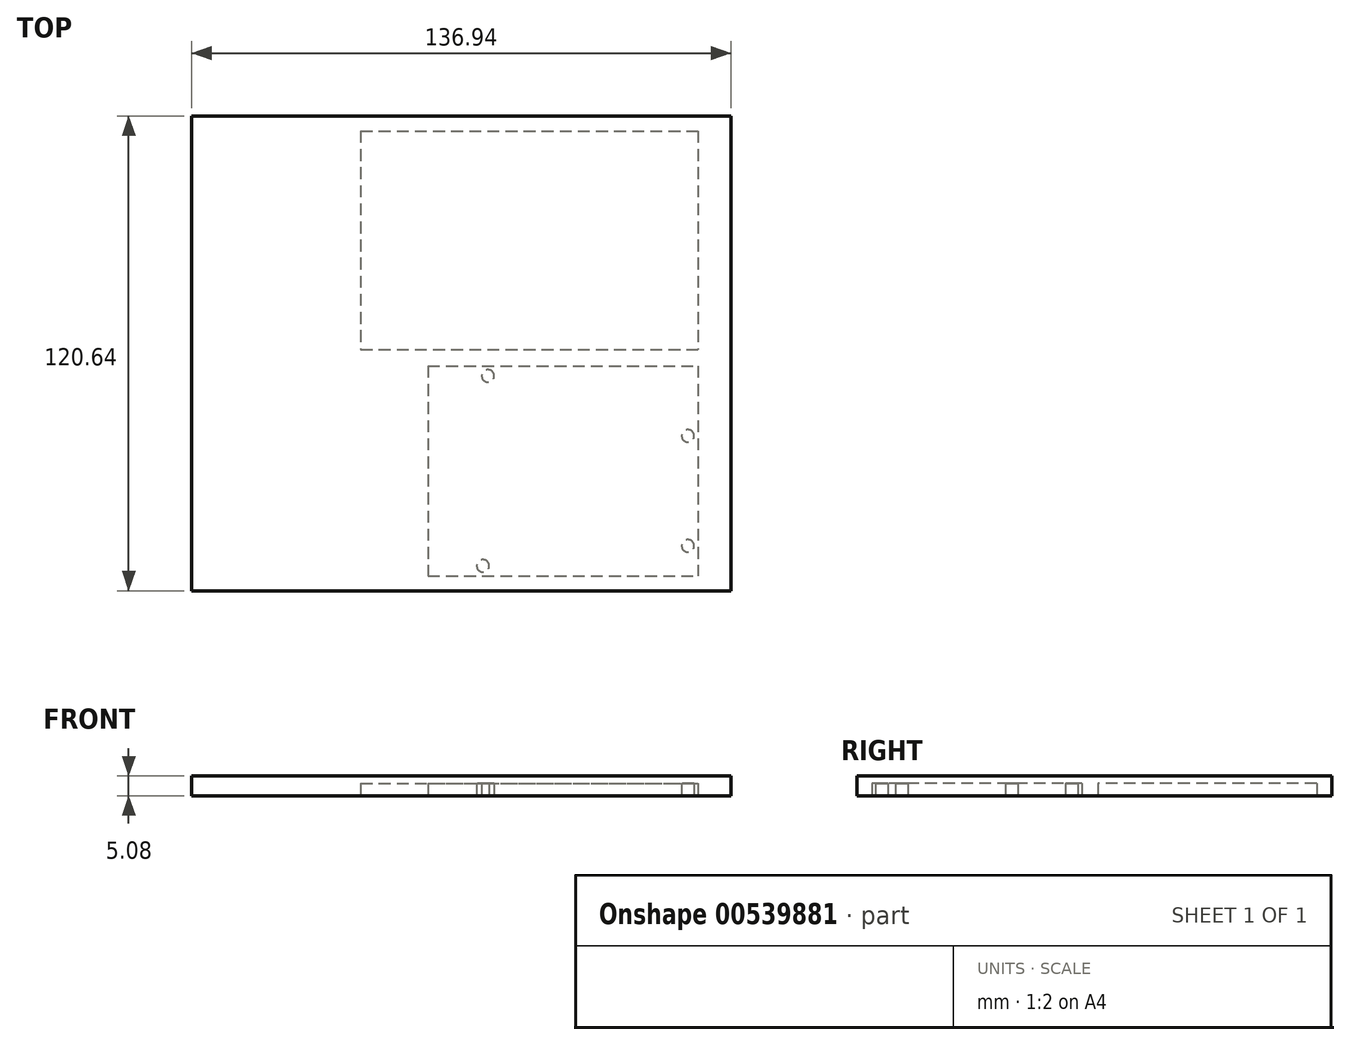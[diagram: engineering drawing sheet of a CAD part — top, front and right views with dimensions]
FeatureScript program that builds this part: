
annotation { "Feature Type Name" : "Feature", "Feature Type Description" : "" }
export const myFeature = defineFeature(function(context is Context, id is Id, definition is map)
    precondition{}
    {
        {
            var Q0;
            Q0=qCreatedBy(makeId("Top.planeOp"),FACE);
            var sketch = newSketch(context, id + "F0", { "sketchPlane" : qUnion([Q0])});
            skLineSegment(sketch, "E0.bottom", {"start": v(68.47, 60.32) * mm, "end": v(-68.47, 60.33) * mm});
            skLineSegment(sketch, "E0.top", {"start": v(68.47, -60.33) * mm, "end": v(-68.47, -60.32) * mm});
            skLineSegment(sketch, "E0.left", {"start": v(68.47, 60.32) * mm, "end": v(68.47, -60.33) * mm});
            skLineSegment(sketch, "E0.right", {"start": v(-68.47, 60.33) * mm, "end": v(-68.47, -60.32) * mm});
            skSolve(sketch);
        }
        {
            var Q0;
            Q0=qCreatedBy(makeId("Top.planeOp"),FACE);
            var sketch = newSketch(context, id + "F1", { "sketchPlane" : qUnion([Q0])});
            skLineSegment(sketch, "E1.bottom", {"start": v(-25.57, 56.52) * mm, "end": v(60.15, 56.52) * mm});
            skLineSegment(sketch, "E1.top", {"start": v(-25.57, 0.95) * mm, "end": v(60.15, 0.95) * mm});
            skLineSegment(sketch, "E1.left", {"start": v(-25.57, 56.52) * mm, "end": v(-25.57, 0.95) * mm});
            skLineSegment(sketch, "E1.right", {"start": v(60.15, 56.52) * mm, "end": v(60.15, 0.95) * mm});
            skLineSegment(sketch, "E2.bottom", {"start": v(-8.48, -3.17) * mm, "end": v(60.1, -3.17) * mm});
            skLineSegment(sketch, "E2.top", {"start": v(-8.48, -56.52) * mm, "end": v(60.1, -56.52) * mm});
            skLineSegment(sketch, "E2.left", {"start": v(-8.48, -3.17) * mm, "end": v(-8.48, -56.52) * mm});
            skLineSegment(sketch, "E2.right", {"start": v(60.1, -3.17) * mm, "end": v(60.1, -56.52) * mm});
            skCircle(sketch, "E3", {"center": v(5.5, -53.98) * mm, "radius": 1.59 * mm});
            skCircle(sketch, "E4", {"center": v(6.76, -5.72) * mm, "radius": 1.59 * mm});
            skCircle(sketch, "E5", {"center": v(57.56, -20.96) * mm, "radius": 1.59 * mm});
            skCircle(sketch, "E6", {"center": v(57.56, -48.9) * mm, "radius": 1.59 * mm});
            skSolve(sketch);
        }
        {
            var Q0;
            Q0=makeQuery(id+"F0.imprint","IMPRINT",FACE,{"disambiguationData":[TD([[makeQuery(id+"F0.imprint","IMPRINT",EDGE,{"derivedFrom":sQuery(id+"F0.wireOp",EDGE,"E0.bottom")}),1.0]])]});
            extrude(context, id + "F2", {"entities" : qUnion([Q0]), "depth" : 5.08 * mm, "offsetDistance" : 25.4 * mm});
        }
        {
            var Q0;
            Q0 = qSketchRegion(id + "F1", true);
            extrude(context, id + "F3", {"entities" : qUnion([Q0]), "operationType" : NewBodyOperationType.REMOVE, "depth" : 3.17 * mm, "offsetDistance" : 25.4 * mm});
        }
        {
            var Q0;
            Q0=sQuery(id+"F1.wireOp",EDGE,"E4");
            var Q1;
            Q1=sQuery(id+"F1.wireOp",EDGE,"E3");
            var Q2;
            Q2=sQuery(id+"F1.wireOp",EDGE,"E5");
            var Q3;
            Q3=sQuery(id+"F1.wireOp",EDGE,"E6");
            extrude(context, id + "F4", {"bodyType" : ToolBodyType.SURFACE, "surfaceEntities" : qUnion([Q0, Q1, Q2, Q3]), "oppositeDirection" : true, "depth" : 12.7 * mm, "offsetDistance" : 25.4 * mm});
        }
    });
